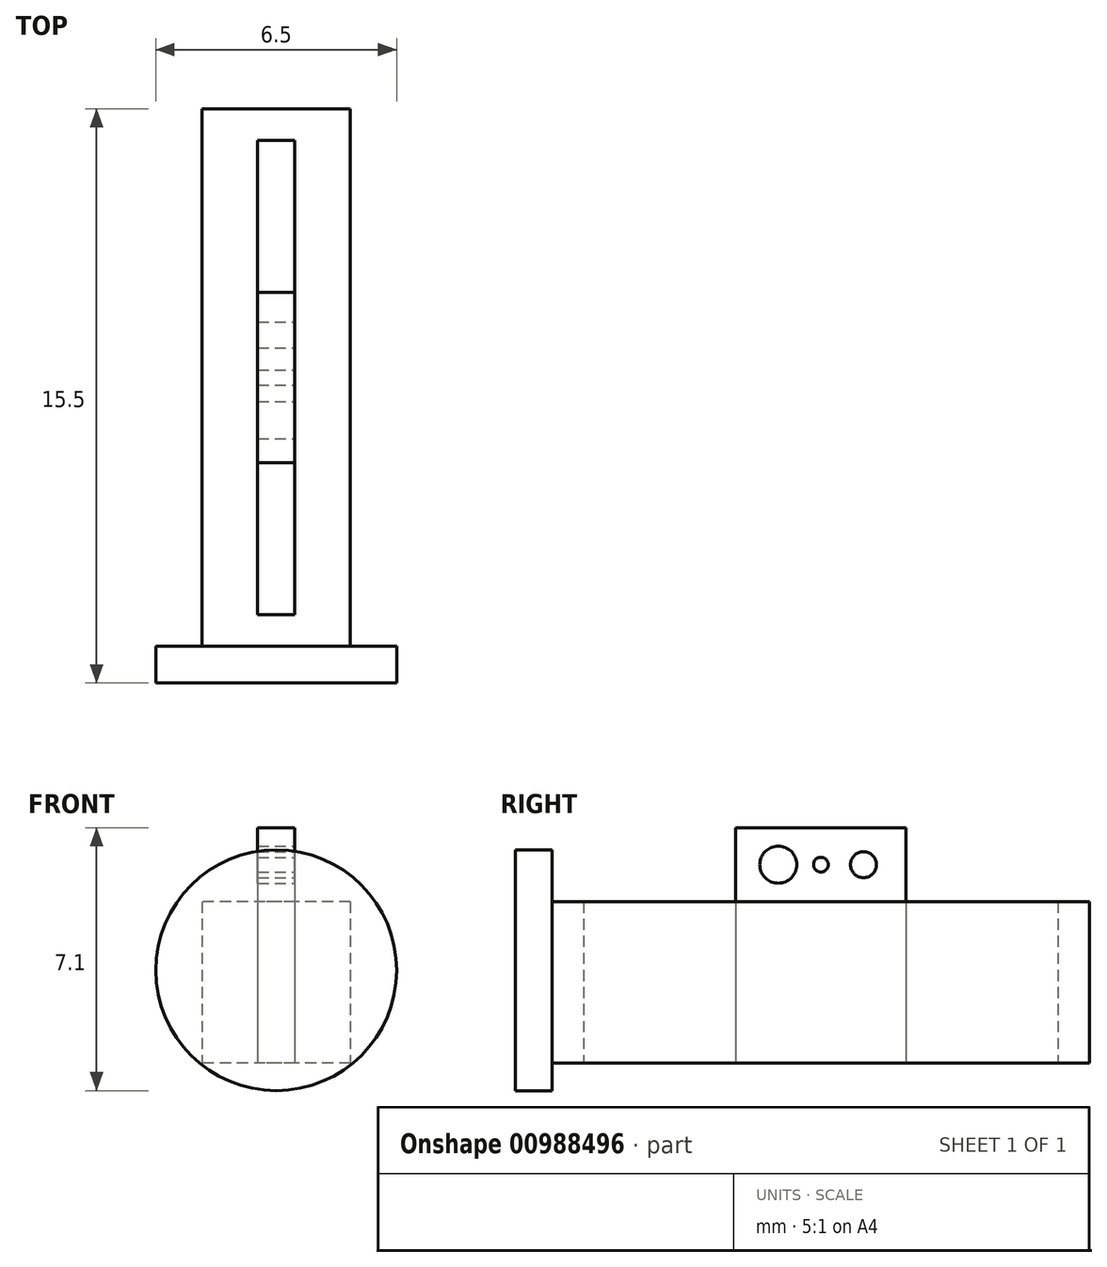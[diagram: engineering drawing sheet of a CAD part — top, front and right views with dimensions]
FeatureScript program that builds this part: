
annotation { "Feature Type Name" : "Feature", "Feature Type Description" : "" }
export const myFeature = defineFeature(function(context is Context, id is Id, definition is map)
    precondition{}
    {
        {
            var Q0;
            Q0=qCreatedBy(makeId("Top.planeOp"),FACE);
            var sketch = newSketch(context, id + "F0", { "sketchPlane" : qUnion([Q0])});
            skLineSegment(sketch, "E0.bottom", {"start": v(2, 7.25) * mm, "end": v(-2, 7.25) * mm});
            skLineSegment(sketch, "E0.top", {"start": v(2, -7.25) * mm, "end": v(-2, -7.25) * mm});
            skLineSegment(sketch, "E0.left", {"start": v(2, 7.25) * mm, "end": v(2, -7.25) * mm});
            skLineSegment(sketch, "E0.right", {"start": v(-2, 7.25) * mm, "end": v(-2, -7.25) * mm});
            skPoint(sketch, "E0.middle", {"position": v(0, 0) * mm});
            skLineSegment(sketch, "E1.bottom", {"start": v(0.5, 6.4) * mm, "end": v(-0.5, 6.4) * mm});
            skLineSegment(sketch, "E1.top", {"start": v(0.5, -6.4) * mm, "end": v(-0.5, -6.4) * mm});
            skLineSegment(sketch, "E1.left", {"start": v(0.5, 6.4) * mm, "end": v(0.5, -6.4) * mm});
            skLineSegment(sketch, "E1.right", {"start": v(-0.5, 6.4) * mm, "end": v(-0.5, -6.4) * mm});
            skLineSegment(sketch, "E2.bottom", {"start": v(0.5, 2.3) * mm, "end": v(-0.5, 2.3) * mm});
            skLineSegment(sketch, "E2.top", {"start": v(0.5, -2.3) * mm, "end": v(-0.5, -2.3) * mm});
            skLineSegment(sketch, "E2.left", {"start": v(0.5, 2.3) * mm, "end": v(0.5, -2.3) * mm});
            skLineSegment(sketch, "E2.right", {"start": v(-0.5, 2.3) * mm, "end": v(-0.5, -2.3) * mm});
            skSolve(sketch);
        }
        {
            var Q0;
            Q0=makeQuery(id+"F0.imprint","IMPRINT",FACE,{"disambiguationData":[TD([[makeQuery(id+"F0.imprint","IMPRINT",EDGE,{"derivedFrom":sQuery(id+"F0.wireOp",EDGE,"E0.bottom")}),1.0]])]});
            extrude(context, id + "F1", {"entities" : qUnion([Q0]), "depth" : 5 * mm - .65 * mm, "offsetDistance" : 25 * mm});
        }
        {
            var Q0;
            {var subQ0=sQuery(id+"F0.wireOp",EDGE,"E2.bottom");Q0=makeQuery(id+"F0.imprint","IMPRINT",FACE,{"disambiguationData":[TD([[makeQuery(id+"F0.imprint","IMPRINT",EDGE,{"derivedFrom":subQ0}),1.0]])]});}
            extrude(context, id + "F2", {"entities" : qUnion([Q0]), "depth" : 7 * mm - .65 * mm, "offsetDistance" : 25 * mm});
        }
        {
            var Q0;
            Q0=makeQuery(id+"F2.opExtrude","SWEPT_FACE",FACE,{"disambiguationData":[OSD([sQuery(id+"F0.wireOp",EDGE,"E1.left")])]});
            var sketch = newSketch(context, id + "F3", { "sketchPlane" : qUnion([Q0])});
            skCircle(sketch, "E3", {"center": v(0, 5.35) * mm, "radius": 0.2 * mm});
            skCircle(sketch, "E4", {"center": v(1.15, 5.35) * mm, "radius": 0.35 * mm});
            skCircle(sketch, "E5", {"center": v(-1.15, 5.35) * mm, "radius": 0.5 * mm});
            skLineSegment(sketch, "E6", {"start": v(1.15, 5.35) * mm, "end": v(2.3, 5.35) * mm, "construction": true});
            skLineSegment(sketch, "E7", {"start": v(1.15, 5.35) * mm, "end": v(0, 5.35) * mm, "construction": true});
            skLineSegment(sketch, "E8", {"start": v(-1.15, 5.35) * mm, "end": v(0, 5.35) * mm, "construction": true});
            skLineSegment(sketch, "E9", {"start": v(0, 4.35) * mm, "end": v(0, 5.35) * mm, "construction": true});
            skLineSegment(sketch, "E10", {"start": v(0, 5.35) * mm, "end": v(0, 6.35) * mm, "construction": true});
            skSolve(sketch);
        }
        {
            var Q0;
            Q0=makeQuery(id+"F1.opExtrude","SWEPT_FACE",FACE,{"disambiguationData":[OSD([sQuery(id+"F0.wireOp",EDGE,"E0.top")])]});
            var sketch = newSketch(context, id + "F4", { "sketchPlane" : qUnion([Q0])});
            skCircle(sketch, "E11", {"center": v(0, 2.5) * mm, "radius": 3.25 * mm});
            skSolve(sketch);
        }
        {
            var Q0;
            Q0=makeQuery(id+"F4.imprint","IMPRINT",FACE,{"disambiguationData":[TD([[makeQuery(id+"F4.imprint","IMPRINT",EDGE,{"derivedFrom":sQuery(id+"F4.wireOp",EDGE,"E11")}),1.0]])]});
            var Q1;
            {var subQ0=sQuery(id+"F0.wireOp",EDGE,"E0.top");Q1=makeQuery(id+"F4.imprint","IMPRINT",FACE,{"disambiguationData":[TD([[makeQuery(id+"F4.imprint","IMPRINT",EDGE,{"derivedFrom":makeQuery(id+"F1.opExtrude","CAP_EDGE",EDGE,{"disambiguationData":[OSD([subQ0])],"isStart":true})}),-1.0]])]});}
            extrude(context, id + "F5", {"entities" : qUnion([Q0, Q1]), "operationType" : NewBodyOperationType.ADD, "depth" : 1 * mm, "offsetDistance" : 25 * mm});
        }
        {
            var Q0;
            Q0=makeQuery(id+"F3.imprint","IMPRINT",FACE,{"disambiguationData":[TD([[makeQuery(id+"F3.imprint","IMPRINT",EDGE,{"derivedFrom":sQuery(id+"F3.wireOp",EDGE,"E5")}),1.0]])]});
            var Q1;
            Q1=makeQuery(id+"F3.imprint","IMPRINT",FACE,{"disambiguationData":[TD([[makeQuery(id+"F3.imprint","IMPRINT",EDGE,{"derivedFrom":sQuery(id+"F3.wireOp",EDGE,"E3")}),1.0]])]});
            var Q2;
            Q2=makeQuery(id+"F3.imprint","IMPRINT",FACE,{"disambiguationData":[TD([[makeQuery(id+"F3.imprint","IMPRINT",EDGE,{"derivedFrom":sQuery(id+"F3.wireOp",EDGE,"E4")}),1.0]])]});
            extrude(context, id + "F6", {"entities" : qUnion([Q0, Q1, Q2]), "operationType" : NewBodyOperationType.REMOVE, "endBound" : BoundingType.THROUGH_ALL, "oppositeDirection" : true, "depth" : 25 * mm, "offsetDistance" : 25 * mm});
        }
    });
